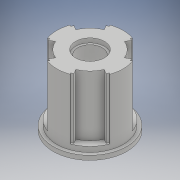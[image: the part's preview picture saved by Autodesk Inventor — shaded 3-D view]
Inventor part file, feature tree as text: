
AUTODESK INVENTOR PART (.ipt)
format: ipt  version: 2017 (Build 210142000, 142)  size: 234,496 bytes
history: native  units: mm
features: sketch x9, other x7, extrude x6, revolve x1, projected_geometry x1
ambient origin geometry x8: Origin, YZ Plane, XZ Plane, XY Plane, X Axis, Y Axis, Z Axis, Center Point
bodies: Body1 (feature_tree)
feature tree (24):
  other  "Твердое тело1"
  extrude  "Выдавливание1"  Depth=16.8mm
  extrude  "Выдавливание2"  Depth=1.0mm TaperAngle=0.0deg
  extrude  "Выдавливание3"  Depth=15.2mm
  extrude  "Выдавливание4"  Depth=1.2mm TaperAngle=0.0deg
  other  "Комбинировать1"
  sketch  "Эскиз5"
  other  "РабПлоскость1"
  sketch  "Эскиз6"
  revolve  "Вращение1"
  other  "Комбинировать2"
  extrude  "Выдавливание5"  Depth=6.4mm
  extrude  "Выдавливание6"  TaperAngle=45.0deg  [1 undecoded]
  other  "РабПлоскость2"
  sketch  "Эскиз1"
  sketch  "Эскиз2"
  sketch  "Эскиз3"
  projected_geometry  "Спроецированная петля1"
  other  "Твердое тело2"
  sketch  "Эскиз4"
  sketch  "Эскиз7"
  other  "Твердое тело3"
  sketch  "Эскиз8"
  sketch  "Эскиз9"
note: 1 required parameter value undecoded (feature->parameter linkage not recoverable at this tier; creation-order binding heuristic only, values carry confidence <= 0.55)
